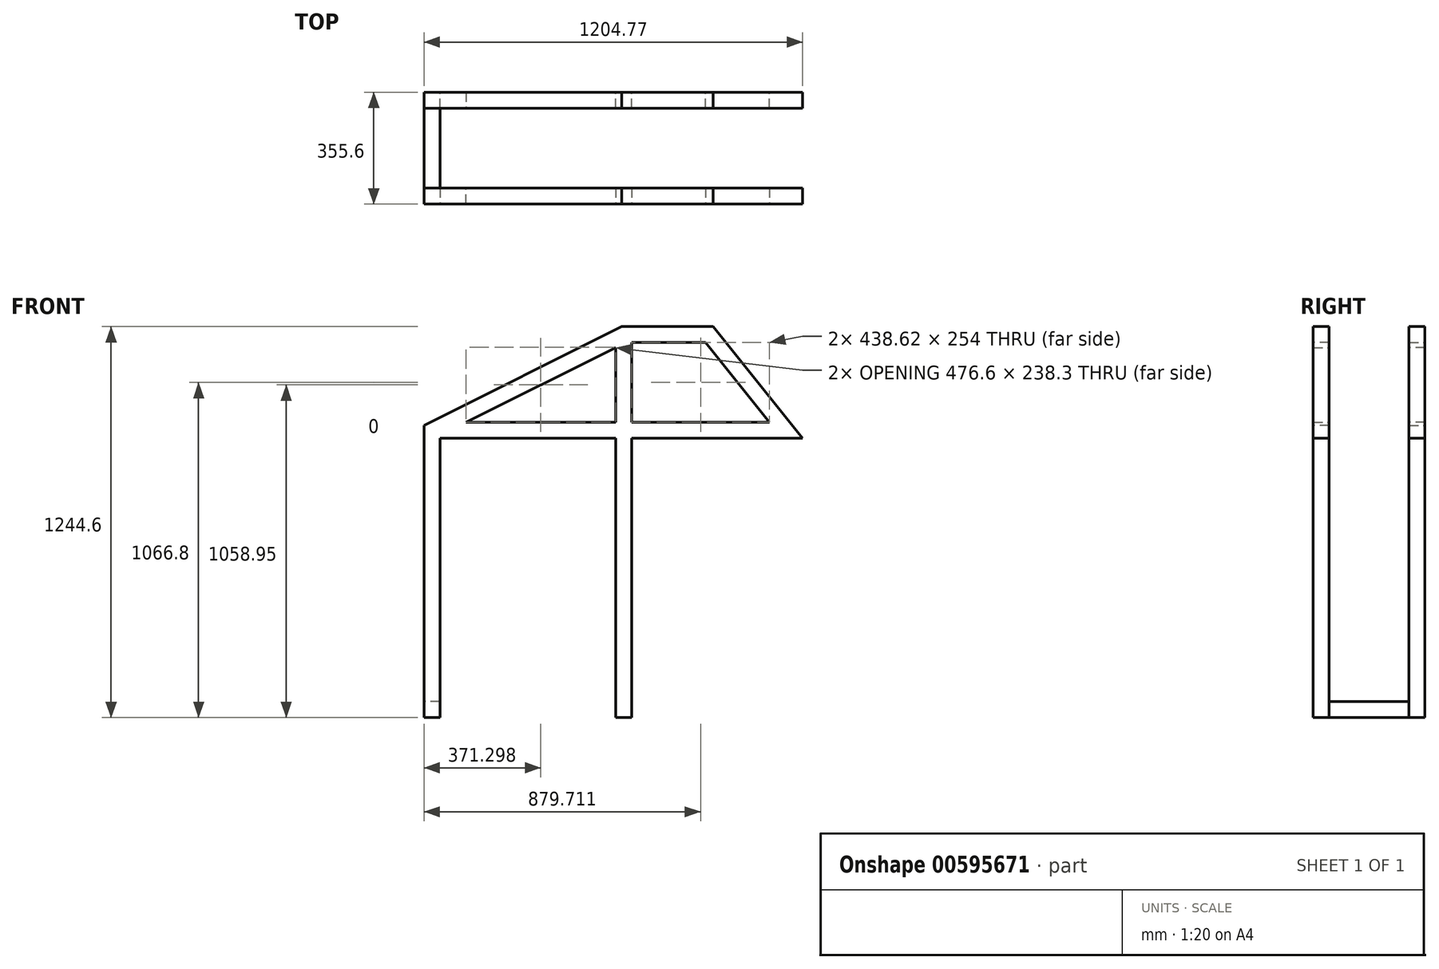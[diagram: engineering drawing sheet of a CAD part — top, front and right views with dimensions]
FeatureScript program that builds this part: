
annotation { "Feature Type Name" : "Feature", "Feature Type Description" : "" }
export const myFeature = defineFeature(function(context is Context, id is Id, definition is map)
    precondition{}
    {
        {
            var Q0;
            Q0=qCreatedBy(makeId("Front.planeOp"),FACE);
            var sketch = newSketch(context, id + "F0", { "sketchPlane" : qUnion([Q0])});
            skLineSegment(sketch, "E0", {"start": v(0, 0) * mm, "end": v(0, 914.4) * mm});
            skLineSegment(sketch, "E1", {"start": v(0, 914.4) * mm, "end": v(609.6, 914.4) * mm});
            skLineSegment(sketch, "E2", {"start": v(0, 914.4) * mm, "end": v(609.6, 1219.2) * mm});
            skLineSegment(sketch, "E3", {"start": v(609.6, 1219.2) * mm, "end": v(609.6, 0) * mm});
            skLineSegment(sketch, "E4", {"start": v(609.6, 914.4) * mm, "end": v(1126.5, 914.4) * mm});
            skLineSegment(sketch, "E5", {"start": v(1126.5, 914.4) * mm, "end": v(882.47, 1219.2) * mm});
            skLineSegment(sketch, "E6", {"start": v(882.47, 1219.2) * mm, "end": v(609.6, 1219.2) * mm});
            skSolve(sketch);
        }
        {
            var Q0;
            Q0=qCreatedBy(makeId("Top.planeOp"),FACE);
            var sketch = newSketch(context, id + "F1", { "sketchPlane" : qUnion([Q0])});
            skLineSegment(sketch, "E7.bottom", {"start": v(-25.4, -25.4) * mm, "end": v(25.4, -25.4) * mm});
            skLineSegment(sketch, "E7.top", {"start": v(-25.4, 25.4) * mm, "end": v(25.4, 25.4) * mm});
            skLineSegment(sketch, "E7.left", {"start": v(-25.4, -25.4) * mm, "end": v(-25.4, 25.4) * mm});
            skLineSegment(sketch, "E7.right", {"start": v(25.4, -25.4) * mm, "end": v(25.4, 25.4) * mm});
            skSolve(sketch);
        }
        {
            var Q0;
            Q0 = qSketchRegion(id + "F1", true);
            var Q1;
            Q1=sQuery(id+"F0.wireOp",EDGE,"E0");
            var Q2;
            Q2=sQuery(id+"F0.wireOp",EDGE,"E2");
            var Q3;
            Q3=sQuery(id+"F0.wireOp",EDGE,"E3");
            sweep(context, id + "F2", {"profiles" : qUnion([Q0]), "path" : qUnion([Q1, Q2, Q3])});
        }
        {
            var Q0;
            Q0=qCreatedBy(makeId("Right.planeOp"),FACE);
            var sketch = newSketch(context, id + "F3", { "sketchPlane" : qUnion([Q0])});
            skLineSegment(sketch, "E8.bottom", {"start": v(25.4, 939.8) * mm, "end": v(-25.4, 939.8) * mm});
            skLineSegment(sketch, "E8.top", {"start": v(25.4, 889) * mm, "end": v(-25.4, 889) * mm});
            skLineSegment(sketch, "E8.left", {"start": v(25.4, 939.8) * mm, "end": v(25.4, 889) * mm});
            skLineSegment(sketch, "E8.right", {"start": v(-25.4, 939.8) * mm, "end": v(-25.4, 889) * mm});
            skLineSegment(sketch, "E9", {"start": v(0, 914.4) * mm, "end": v(-142.79, 914.4) * mm, "construction": true});
            skSolve(sketch);
        }
        {
            var Q0;
            Q0 = qSketchRegion(id + "F3", true);
            var Q1;
            Q1=sQuery(id+"F0.wireOp",EDGE,"E1");
            var Q2;
            Q2=sQuery(id+"F0.wireOp",EDGE,"E4");
            var Q3;
            Q3=sQuery(id+"F0.wireOp",EDGE,"E5");
            var Q4;
            Q4=sQuery(id+"F0.wireOp",EDGE,"E6");
            sweep(context, id + "F4", {"operationType" : NewBodyOperationType.ADD, "profiles" : qUnion([Q0]), "path" : qUnion([Q1, Q2, Q3, Q4])});
        }
        {
            var Q0;
            Q0=qCreatedBy(makeId("Front.planeOp"),FACE);
            var sketch = newSketch(context, id + "F5", { "sketchPlane" : qUnion([Q0])});
            skLineSegment(sketch, "E10.0", {"start": v(635, 1244.6) * mm, "end": v(603.6, 1244.6) * mm});
            skPoint(sketch, "E11.0.end.orphan", {"position": v(609.6, 1219.2) * mm});
            skPoint(sketch, "E11.0.start.orphan", {"position": v(882.47, 1219.2) * mm});
            skLineSegment(sketch, "E12.0", {"start": v(603.6, 1244.6) * mm, "end": v(635, 1260.3) * mm});
            skPoint(sketch, "E13.orphan", {"position": v(635, 1244.6) * mm});
            skPoint(sketch, "E14.orphan", {"position": v(-25.4, 930.1) * mm});
            skPoint(sketch, "E15.orphan", {"position": v(894.67, 1244.6) * mm});
            skLineSegment(sketch, "E16.0", {"start": v(635, 1260.3) * mm, "end": v(635, 1244.6) * mm});
            skSolve(sketch);
        }
        {
            var Q0;
            Q0 = qSketchRegion(id + "F5", true);
            extrude(context, id + "F6", {"entities" : qUnion([Q0]), "operationType" : NewBodyOperationType.REMOVE, "endBound" : BoundingType.THROUGH_ALL, "oppositeDirection" : true, "depth" : 25.4 * mm, "offsetDistance" : 25.4 * mm, "hasSecondDirection" : true, "secondDirectionBound" : SecondDirectionBoundingType.THROUGH_ALL, "secondDirectionOppositeDirection" : false, "secondDirectionDepth" : 25.4 * mm});
        }
        {
            var Q0;
            Q0=qCreatedBy(makeId("Front.planeOp"),FACE);
            cPlane(context, id + "F7", {"entities" : qUnion([Q0]), "cplaneType" : CPlaneType.OFFSET, "offset" : 152.4 * mm, "width" : 152.4 * mm, "height" : 152.4 * mm});
        }
        {
            var Q0;
            Q0=makeQuery(id+"F2.opSweep","SWEPT_BODY",BODY,{"disambiguationData":[OSD([sQuery(id+"F0.wireOp",EDGE,"E3"),sQuery(id+"F1.wireOp",EDGE,"E7.bottom"),sQuery(id+"F1.wireOp",EDGE,"E7.top"),sQuery(id+"F1.wireOp",EDGE,"E7.left"),sQuery(id+"F1.wireOp",EDGE,"E7.right")])]});
            var Q1;
            Q1=qCreatedBy(id+"F7.planeOp",FACE);
            mirror(context, id + "F8", {"entities" : qUnion([Q0]), "mirrorPlane" : qUnion([Q1])});
        }
        {
            var Q0;
            Q0=qCreatedBy(id+"F7.planeOp",FACE);
            var sketch = newSketch(context, id + "F9", { "sketchPlane" : qUnion([Q0])});
            skLineSegment(sketch, "E17.0", {"start": v(25.4, 0) * mm, "end": v(-25.4, 0) * mm});
            skLineSegment(sketch, "E18", {"start": v(-25.4, 0) * mm, "end": v(-25.4, 50.8) * mm});
            skLineSegment(sketch, "E19", {"start": v(-25.4, 50.8) * mm, "end": v(25.4, 50.8) * mm});
            skLineSegment(sketch, "E20", {"start": v(25.4, 50.8) * mm, "end": v(25.4, 0) * mm});
            skSolve(sketch);
        }
        {
            var Q0;
            Q0=makeQuery(id+"F9.imprint","IMPRINT",FACE,{"disambiguationData":[TD([[makeQuery(id+"F9.imprint","IMPRINT",EDGE,{"derivedFrom":sQuery(id+"F9.wireOp",EDGE,"E17.0")}),-1.0]])]});
            var Q1;
            Q1=makeQuery(id+"F8.opPattern","COPY",BODY,{"derivedFrom":makeQuery(id+"F2.opSweep","SWEPT_BODY",BODY,{"disambiguationData":[OSD([sQuery(id+"F0.wireOp",EDGE,"E3"),sQuery(id+"F1.wireOp",EDGE,"E7.bottom"),sQuery(id+"F1.wireOp",EDGE,"E7.top"),sQuery(id+"F1.wireOp",EDGE,"E7.left"),sQuery(id+"F1.wireOp",EDGE,"E7.right")])]}),"instanceName":"1"});
            var Q2;
            Q2=makeQuery(id+"F2.opSweep","SWEPT_BODY",BODY,{"disambiguationData":[OSD([sQuery(id+"F0.wireOp",EDGE,"E3"),sQuery(id+"F1.wireOp",EDGE,"E7.bottom"),sQuery(id+"F1.wireOp",EDGE,"E7.top"),sQuery(id+"F1.wireOp",EDGE,"E7.left"),sQuery(id+"F1.wireOp",EDGE,"E7.right")])]});
            extrude(context, id + "F10", {"entities" : qUnion([Q0]), "endBound" : BoundingType.UP_TO_BODY, "depth" : 152.4 * mm, "endBoundEntityBody" : qUnion([Q1]), "offsetDistance" : 25.4 * mm, "hasSecondDirection" : true, "secondDirectionBound" : SecondDirectionBoundingType.UP_TO_BODY, "secondDirectionOppositeDirection" : true, "secondDirectionDepth" : 152.4 * mm, "secondDirectionBoundEntityBody" : qUnion([Q2])});
        }
    });
